# Revit family: Coral 1200
name_source: partatom
category: Lighting Fixtures
revit_build: Autodesk Revit 2017 (Build: 20160225_1515(x64)
units: mm (PartAtom-declared; Revit-internal decimal feet)

## family parameters
Always vertical = Yes
Cut with Voids When Loaded = No
Host = Ceiling
Light Source = Yes
OmniClass Number = 23.80.70.11
OmniClass Title = Luminaries for Internal Lighting
Part Type = Normal
Room Calculation Point = No
Round Connector Dimension = Use Diameter
Shared = No

## types (1)
- Generic
    Apparent Load = 0 VA
    Color Filter = 16777215
    Cordset finish = Plastic, Opaque White
    Description = Pendant in bamboo plywood. Can be made in a large range of colours. Lamp is not supplied
    Dimming Lamp Color Temperature Shift = <None>
    Lamp = E27 / (E26 USA)
    Lamp Wattage = 0 W
    Light Source Symbol Size = 300 mm
    Manufacturer = David Trubridge
    Model = Coral 1200
    Type Comments = Ceilig Rose required, contact supplier for options.
    URL = https://www.davidtrubridge.com
    Wattage Comments = Max. 60 Watts. 110V(US) / 230-240V(EU). Lamp NOT provided.

## geometry (parser evidence)
native form markers: Sweep x3
no freeform markers — native parametric forms only
